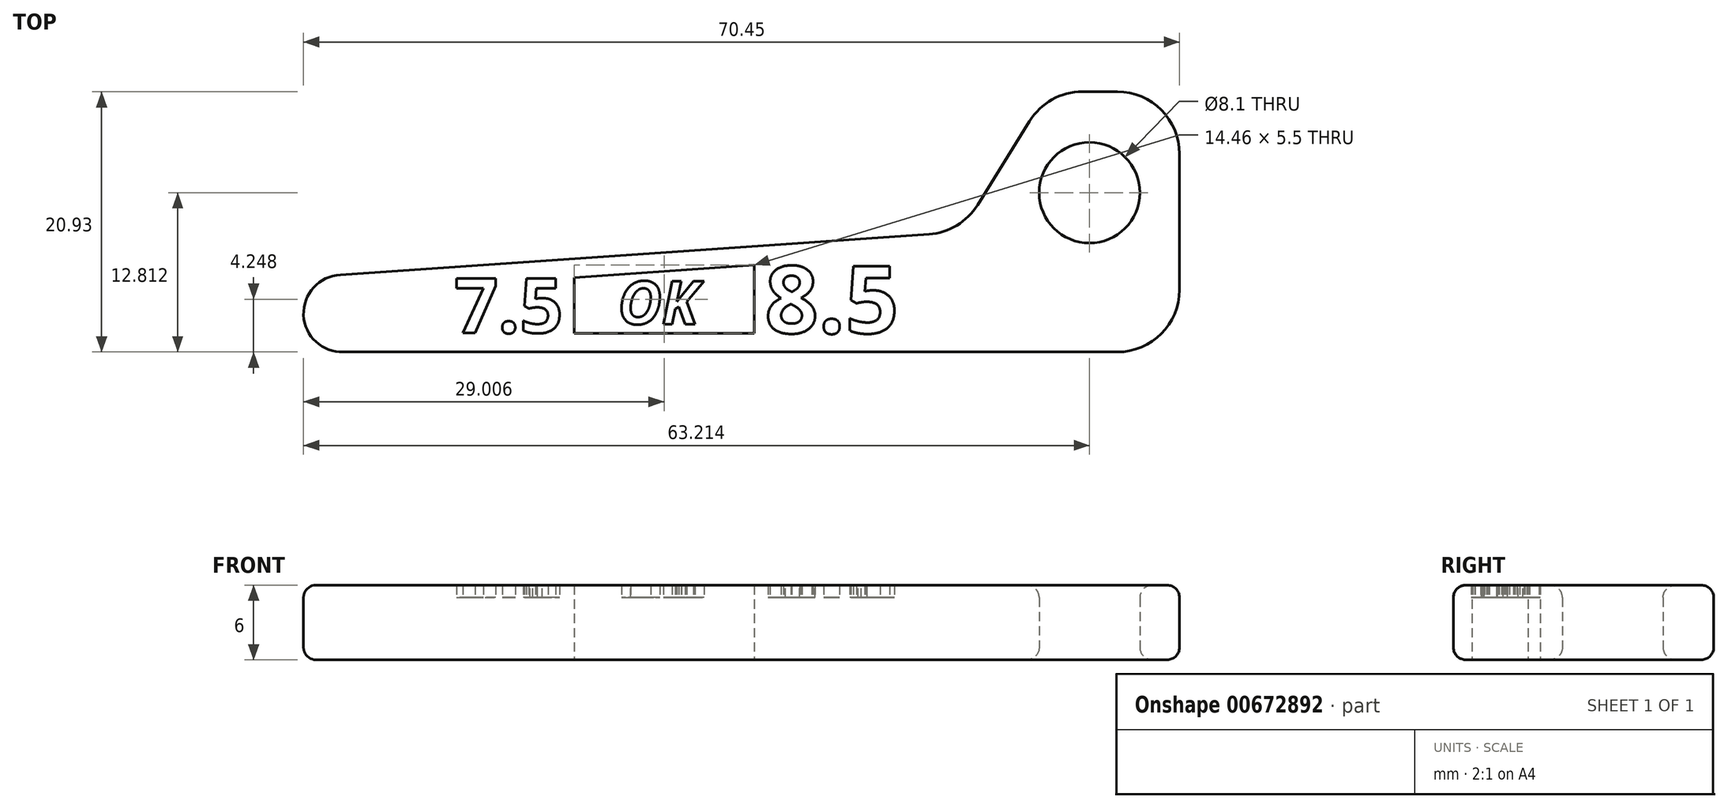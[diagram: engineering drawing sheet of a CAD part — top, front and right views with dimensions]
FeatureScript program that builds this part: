
annotation { "Feature Type Name" : "Feature", "Feature Type Description" : "" }
export const myFeature = defineFeature(function(context is Context, id is Id, definition is map)
    precondition{}
    {
        {
            var Q0;
            Q0=qCreatedBy(makeId("Top.planeOp"),FACE);
            var sketch = newSketch(context, id + "F0", { "sketchPlane" : qUnion([Q0])});
            skLineSegment(sketch, "E0", {"start": v(-15.9, 0) * mm, "end": v(34.1, 0) * mm});
            skLineSegment(sketch, "E1", {"start": v(-16.15, 6.2) * mm, "end": v(31.17, 9.47) * mm});
            skLineSegment(sketch, "E2", {"start": v(2.64, 1.5) * mm, "end": v(2.64, 6) * mm});
            skLineSegment(sketch, "E3", {"start": v(17.1, 1.5) * mm, "end": v(17.1, 7) * mm});
            skPoint(sketch, "E4.third.point", {"position": v(-19.1, 3.06) * mm});
            skArc(sketch, "E5", {"start": v(-16.15, 6.2) * mm, "mid": v(-19.12, 2.97) * mm, "end": v(-15.9, 0) * mm});
            skLineSegment(sketch, "E6", {"start": v(35.08, 11.83) * mm, "end": v(39.26, 18.57) * mm});
            skLineSegment(sketch, "E7", {"start": v(43.5, 20.93) * mm, "end": v(46.32, 20.93) * mm});
            skLineSegment(sketch, "E8", {"start": v(51.32, 15.93) * mm, "end": v(51.32, 5) * mm});
            skLineSegment(sketch, "E9", {"start": v(46.32, 0) * mm, "end": v(34.1, 0) * mm});
            skPoint(sketch, "E10.visualSharp", {"position": v(40.72, 20.93) * mm});
            skArc(sketch, "E10.filletArc", {"start": v(43.5, 20.93) * mm, "mid": v(41.07, 20.3) * mm, "end": v(39.26, 18.57) * mm});
            skPoint(sketch, "E11.visualSharp", {"position": v(51.32, 20.93) * mm});
            skArc(sketch, "E11.filletArc", {"start": v(51.32, 15.93) * mm, "mid": v(49.86, 19.47) * mm, "end": v(46.32, 20.93) * mm});
            skPoint(sketch, "E12.visualSharp", {"position": v(51.32, 0) * mm});
            skArc(sketch, "E12.filletArc", {"start": v(46.32, 0) * mm, "mid": v(49.86, 1.46) * mm, "end": v(51.32, 5) * mm});
            skPoint(sketch, "E13.visualSharp", {"position": v(33.73, 9.65) * mm});
            skArc(sketch, "E13.filletArc", {"start": v(31.17, 9.47) * mm, "mid": v(33.4, 10.18) * mm, "end": v(35.08, 11.83) * mm});
            skCircle(sketch, "E14", {"center": v(44.08, 12.81) * mm, "radius": 4.05 * mm});
            skLineSegment(sketch, "E15.4", {"start": v(2.64, 6) * mm, "end": v(17.1, 7) * mm});
            skLineSegment(sketch, "E15.9", {"start": v(2.64, 1.5) * mm, "end": v(17.1, 1.5) * mm});
            skText(sketch, "E16", { "text": "7.5", "fontName": "OpenSans-Bold.ttf"});
            skText(sketch, "E17", { "text": "8.5", "fontName": "OpenSans-Bold.ttf"});
            skText(sketch, "E18", { "text": "OK", "fontName": "OpenSans-BoldItalic.ttf"});
            const initialGuessF0  = {"E16": [-0.00698, 0.00155, 1, 0, 0.0044], "E17": [0.01797, 0.00152, 1, 0, 0.00543], "E18": [0.00616, 0.00224, 1, 0, 0.00347]};
            skSetInitialGuess(sketch, initialGuessF0);
            skSolve(sketch);
        }
        {
            var Q0;
            {var subQ5=sQuery(id+"F0.wireOp",EDGE,"E5");Q0=makeQuery(id+"F0.imprint","IMPRINT",FACE,{"disambiguationData":[TD([[makeQuery(id+"F0.imprint","IMPRINT",EDGE,{"derivedFrom":subQ5}),1.0]])]});}
            var Q1;
            {var subQ5=sQuery(id+"F0.wireOp",EDGE,"E15.4");Q1=makeQuery(id+"F0.imprint","IMPRINT",FACE,{"disambiguationData":[TD([[makeQuery(id+"F0.imprint","IMPRINT",EDGE,{"derivedFrom":subQ5}),1.0]])]});}
            var Q2;
            {var subQ5=sQuery(id+"F0.wireOp",EDGE,"E15.9");Q2=makeQuery(id+"F0.imprint","IMPRINT",FACE,{"disambiguationData":[TD([[makeQuery(id+"F0.imprint","IMPRINT",EDGE,{"derivedFrom":subQ5}),-1.0]])]});}
            var Q3;
            Q3=makeQuery(id+"F0.imprint","IMPRINT",FACE,{"disambiguationData":[TD([[makeQuery(id+"F0.imprint","IMPRINT",EDGE,{"derivedFrom":sQuery(id+"F0.wireOp",EDGE,"E6")}),-1.0]])]});
            extrude(context, id + "F1", {"entities" : qUnion([Q0, Q1, Q2, Q3]), "depth" : 6 * mm, "offsetDistance" : 25 * mm});
        }
        {
            var Q0;
            Q0=makeQuery(id+"F1.opExtrude","SWEPT_FACE",FACE,{"disambiguationData":[OSD([sQuery(id+"F0.wireOp",EDGE,"E1")])]});
            var Q1;
            Q1=makeQuery(id+"F1.opExtrude","SWEPT_FACE",FACE,{"disambiguationData":[OSD([sQuery(id+"F0.wireOp",EDGE,"E5")])]});
            var Q2;
            Q2=makeQuery(id+"F1.opExtrude","SWEPT_FACE",FACE,{"disambiguationData":[OSD([sQuery(id+"F0.wireOp",EDGE,"E6")])]});
            var Q3;
            Q3=makeQuery(id+"F1.opExtrude","SWEPT_FACE",FACE,{"disambiguationData":[OSD([sQuery(id+"F0.wireOp",EDGE,"E13.filletArc")])]});
            var Q4;
            Q4=makeQuery(id+"F1.opExtrude","SWEPT_FACE",FACE,{"disambiguationData":[OSD([sQuery(id+"F0.wireOp",EDGE,"E10.filletArc")])]});
            var Q5;
            Q5=makeQuery(id+"F1.opExtrude","SWEPT_FACE",FACE,{"disambiguationData":[OSD([sQuery(id+"F0.wireOp",EDGE,"E14")])]});
            var Q6;
            Q6=makeQuery(id+"F1.opExtrude","SWEPT_FACE",FACE,{"disambiguationData":[OSD([sQuery(id+"F0.wireOp",EDGE,"E7")])]});
            var Q7;
            Q7=makeQuery(id+"F1.opExtrude","SWEPT_FACE",FACE,{"disambiguationData":[OSD([sQuery(id+"F0.wireOp",EDGE,"E11.filletArc")])]});
            var Q8;
            Q8=makeQuery(id+"F1.opExtrude","SWEPT_FACE",FACE,{"disambiguationData":[OSD([sQuery(id+"F0.wireOp",EDGE,"E8")])]});
            var Q9;
            Q9=makeQuery(id+"F1.opExtrude","SWEPT_FACE",FACE,{"disambiguationData":[OSD([sQuery(id+"F0.wireOp",EDGE,"E12.filletArc")])]});
            var Q10;
            Q10=makeQuery(id+"F1.opExtrude","SWEPT_FACE",FACE,{"disambiguationData":[OSD([sQuery(id+"F0.wireOp",EDGE,"E9")])]});
            var Q11;
            Q11=makeQuery(id+"F1.opExtrude","SWEPT_FACE",FACE,{"disambiguationData":[OSD([sQuery(id+"F0.wireOp",EDGE,"E0")])]});
            fillet(context, id + "F2", {"entities" : qUnion([Q0, Q1, Q2, Q3, Q4, Q5, Q6, Q7, Q8, Q9, Q10, Q11]), "radius" : 1 * mm, "tangentPropagation" : true, "allowEdgeOverflow" : false});
        }
        {
            var Q0;
            {var subQ0=sQuery(id+"F0.wireOp",EDGE,"E15.4");Q0=makeQuery(id+"F0.imprint","IMPRINT",FACE,{"disambiguationData":[TD([[makeQuery(id+"F0.imprint","IMPRINT",EDGE,{"derivedFrom":subQ0}),-1.0]])]});}
            extrude(context, id + "F3", {"entities" : qUnion([Q0]), "depth" : 6 * mm, "offsetDistance" : 25 * mm});
        }
        {
            var Q0;
            Q0=makeQuery(id+"F0.imprint","IMPRINT",FACE,{"disambiguationData":[TD([[makeQuery(id+"F0.imprint","IMPRINT",EDGE,{"derivedFrom":sQuery(id+"F0.wireOp",EDGE,"E16.sketch_text.stroke-0")}),-1.0]])]});
            var Q1;
            Q1=makeQuery(id+"F0.imprint","IMPRINT",FACE,{"disambiguationData":[TD([[makeQuery(id+"F0.imprint","IMPRINT",EDGE,{"derivedFrom":sQuery(id+"F0.wireOp",EDGE,"E16.sketch_text.stroke-15")}),-1.0]])]});
            var Q2;
            Q2=makeQuery(id+"F0.imprint","IMPRINT",FACE,{"disambiguationData":[TD([[makeQuery(id+"F0.imprint","IMPRINT",EDGE,{"derivedFrom":sQuery(id+"F0.wireOp",EDGE,"E17.sketch_text.stroke-0")}),-1.0]])]});
            var Q3;
            Q3=makeQuery(id+"F0.imprint","IMPRINT",FACE,{"disambiguationData":[TD([[makeQuery(id+"F0.imprint","IMPRINT",EDGE,{"derivedFrom":sQuery(id+"F0.wireOp",EDGE,"E17.sketch_text.stroke-39")}),-1.0]])]});
            extrude(context, id + "F4", {"entities" : qUnion([Q0, Q1, Q2, Q3]), "operationType" : NewBodyOperationType.ADD, "depth" : 5 * mm, "offsetDistance" : 25 * mm});
        }
        {
            var Q0;
            Q0=makeQuery(id+"F0.imprint","IMPRINT",FACE,{"disambiguationData":[TD([[makeQuery(id+"F0.imprint","IMPRINT",EDGE,{"derivedFrom":sQuery(id+"F0.wireOp",EDGE,"E16.sketch_text.stroke-7")}),-1.0]])]});
            var Q1;
            Q1=makeQuery(id+"F0.imprint","IMPRINT",FACE,{"disambiguationData":[TD([[makeQuery(id+"F0.imprint","IMPRINT",EDGE,{"derivedFrom":sQuery(id+"F0.wireOp",EDGE,"E17.sketch_text.stroke-31")}),-1.0]])]});
            extrude(context, id + "F5", {"entities" : qUnion([Q0, Q1]), "operationType" : NewBodyOperationType.ADD, "depth" : 5 * mm, "offsetDistance" : 25 * mm});
        }
        {
            var Q0;
            Q0=makeQuery(id+"F0.imprint","IMPRINT",FACE,{"disambiguationData":[TD([[makeQuery(id+"F0.imprint","IMPRINT",EDGE,{"derivedFrom":sQuery(id+"F0.wireOp",EDGE,"E17.sketch_text.stroke-23")}),1.0]])]});
            var Q1;
            Q1=makeQuery(id+"F0.imprint","IMPRINT",FACE,{"disambiguationData":[TD([[makeQuery(id+"F0.imprint","IMPRINT",EDGE,{"derivedFrom":sQuery(id+"F0.wireOp",EDGE,"E17.sketch_text.stroke-16")}),1.0]])]});
            extrude(context, id + "F6", {"entities" : qUnion([Q0, Q1]), "operationType" : NewBodyOperationType.ADD, "depth" : 6 * mm, "offsetDistance" : 25 * mm});
        }
        {
            var Q0;
            Q0=makeQuery(id+"F0.imprint","IMPRINT",FACE,{"disambiguationData":[TD([[makeQuery(id+"F0.imprint","IMPRINT",EDGE,{"derivedFrom":sQuery(id+"F0.wireOp",EDGE,"E18.sketch_text.stroke-0")}),-1.0]])]});
            var Q1;
            Q1=makeQuery(id+"F0.imprint","IMPRINT",FACE,{"disambiguationData":[TD([[makeQuery(id+"F0.imprint","IMPRINT",EDGE,{"derivedFrom":sQuery(id+"F0.wireOp",EDGE,"E18.sketch_text.stroke-20")}),-1.0]])]});
            extrude(context, id + "F7", {"entities" : qUnion([Q0, Q1]), "operationType" : NewBodyOperationType.ADD, "depth" : 5 * mm, "offsetDistance" : 25 * mm});
        }
        {
            var Q0;
            Q0=makeQuery(id+"F0.imprint","IMPRINT",FACE,{"disambiguationData":[TD([[makeQuery(id+"F0.imprint","IMPRINT",EDGE,{"derivedFrom":sQuery(id+"F0.wireOp",EDGE,"E18.sketch_text.stroke-10")}),1.0]])]});
            extrude(context, id + "F8", {"entities" : qUnion([Q0]), "operationType" : NewBodyOperationType.ADD, "depth" : 6 * mm, "offsetDistance" : 25 * mm});
        }
    });
